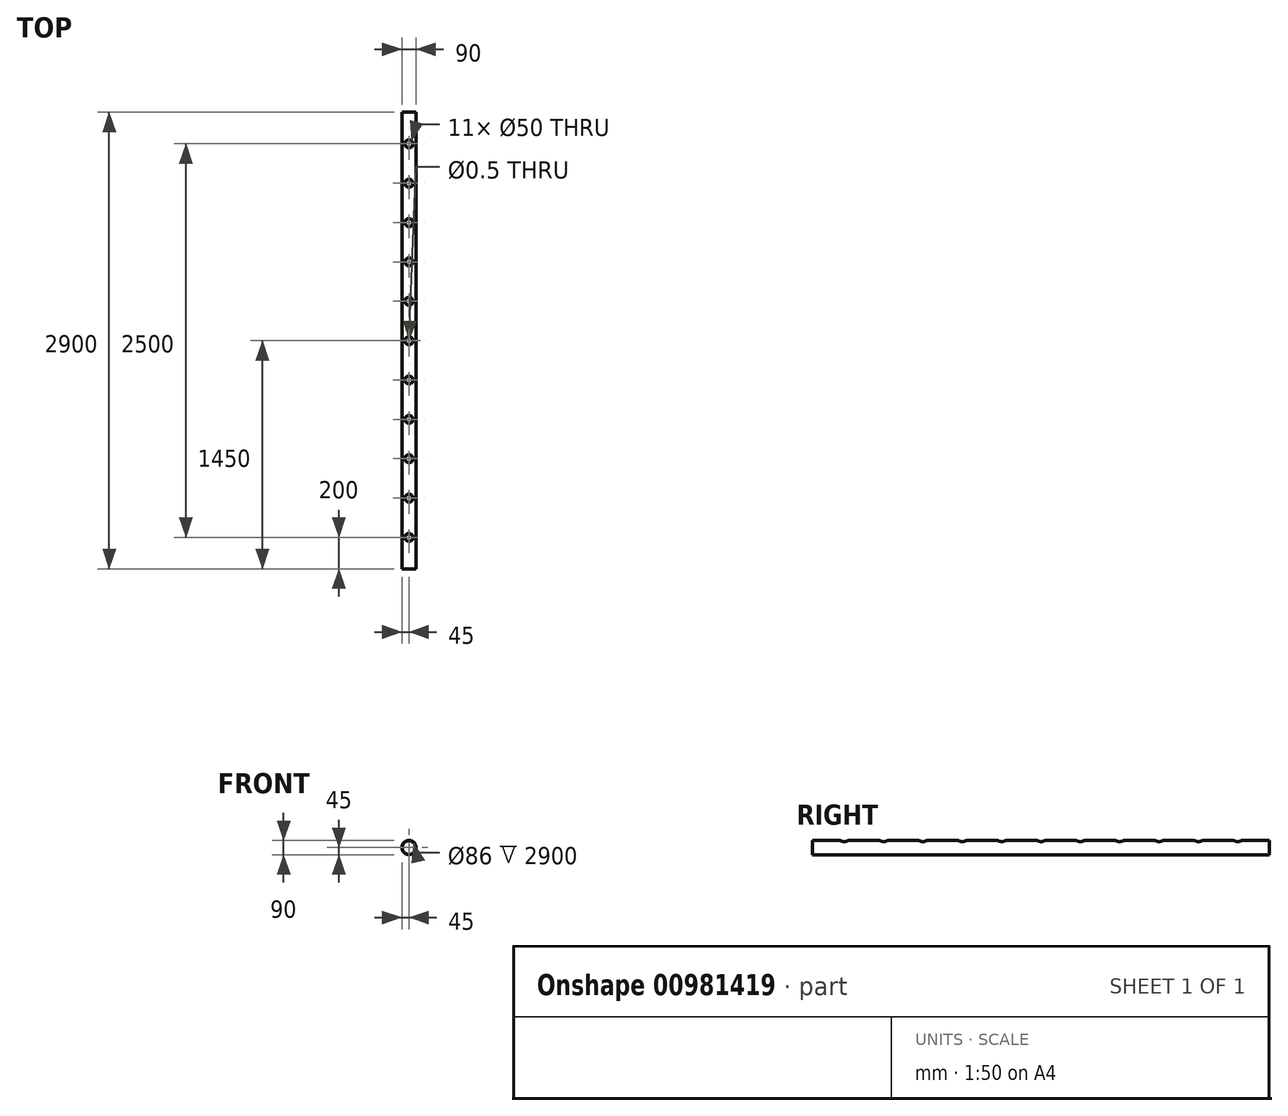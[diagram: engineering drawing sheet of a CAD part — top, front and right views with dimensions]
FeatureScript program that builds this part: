
annotation { "Feature Type Name" : "Feature", "Feature Type Description" : "" }
export const myFeature = defineFeature(function(context is Context, id is Id, definition is map)
    precondition{}
    {
        {
            var Q0;
            Q0=qCreatedBy(makeId("Front.planeOp"),FACE);
            var sketch = newSketch(context, id + "F0", { "sketchPlane" : qUnion([Q0])});
            skCircle(sketch, "E0", {"center": v(0, 0) * mm, "radius": 45 * mm});
            skCircle(sketch, "E1.0", {"center": v(0, 0) * mm, "radius": 43 * mm});
            skSolve(sketch);
        }
        {
            var Q0;
            Q0=qSketchRegion(id+"F0",true);
            extrude(context, id + "F1", {"entities" : qUnion([Q0]), "endBound" : BoundingType.SYMMETRIC, "depth" : 2900 * mm, "offsetDistance" : 25 * mm});
        }
        {
            var Q0;
            Q0=qCreatedBy(makeId("Top.planeOp"),FACE);
            cPlane(context, id + "F2", {"entities" : qUnion([Q0]), "cplaneType" : CPlaneType.OFFSET, "offset" : 45 * mm, "width" : 150 * mm, "height" : 150 * mm});
        }
        {
            var Q0;
            Q0=qCreatedBy(id+"F2.planeOp",FACE);
            var sketch = newSketch(context, id + "F3", { "sketchPlane" : qUnion([Q0])});
            skPoint(sketch, "E2", {"position": v(0, -1250) * mm});
            skPoint(sketch, "E3", {"position": v(0, -1000) * mm});
            skPoint(sketch, "E4", {"position": v(0, -750) * mm});
            skPoint(sketch, "E5", {"position": v(0, -500) * mm});
            skPoint(sketch, "E6", {"position": v(0, -250) * mm});
            skPoint(sketch, "E7", {"position": v(0, 0) * mm});
            skPoint(sketch, "E8", {"position": v(0, 250) * mm});
            skPoint(sketch, "E9", {"position": v(0, 500) * mm});
            skPoint(sketch, "E10", {"position": v(0, 750) * mm});
            skPoint(sketch, "E11", {"position": v(0, 1000) * mm});
            skPoint(sketch, "E12", {"position": v(0, 1250) * mm});
            skSolve(sketch);
        }
        {
            var Q0;
            Q0=sQuery(id+"F3.wireOp",VERTEX,"E2");
            var Q1;
            Q1=sQuery(id+"F3.wireOp",VERTEX,"E3");
            var Q2;
            Q2=sQuery(id+"F3.wireOp",VERTEX,"E4");
            var Q3;
            Q3=sQuery(id+"F3.wireOp",VERTEX,"E5");
            var Q4;
            Q4=sQuery(id+"F3.wireOp",VERTEX,"E6");
            var Q5;
            Q5=sQuery(id+"F3.wireOp",VERTEX,"E7");
            var Q6;
            Q6=sQuery(id+"F3.wireOp",VERTEX,"E8");
            var Q7;
            Q7=sQuery(id+"F3.wireOp",VERTEX,"E9");
            var Q8;
            Q8=sQuery(id+"F3.wireOp",VERTEX,"E10");
            var Q9;
            Q9=sQuery(id+"F3.wireOp",VERTEX,"E11");
            var Q10;
            Q10=sQuery(id+"F3.wireOp",VERTEX,"E12");
            var Q11;
            Q11=sQuery(id+"F3.wireOp",VERTEX,"98bfdb10-889b-4535-8e33-4c68f40e96e9");
            var Q12;
            Q12=sQuery(id+"F3.wireOp",VERTEX,"d6d3cdd6-09bc-4208-8bfb-94afde8f0a46");
            var Q13;
            Q13=sQuery(id+"F3.wireOp",VERTEX,"734153c6-2249-4abd-a6b6-f48a35ac855c");
            var Q14;
            Q14=sQuery(id+"F3.wireOp",VERTEX,"46e0f81d-7a3e-4eb5-89d9-9d338da62cf5");
            var Q15;
            Q15=sQuery(id+"F3.wireOp",VERTEX,"f4cd902c-7ee6-44a1-aa6d-15636b985a91");
            var Q16;
            Q16=sQuery(id+"F3.wireOp",VERTEX,"a0becd45-3f8c-473a-b9c5-eca89ffffb86");
            var Q17;
            Q17=sQuery(id+"F3.wireOp",VERTEX,"449d03d7-6090-459a-adaf-9611daa20e82");
            var Q18;
            Q18=sQuery(id+"F3.wireOp",VERTEX,"1d2369e2-f7b6-45cb-9ac7-ef4d2139859a");
            var Q19;
            Q19=sQuery(id+"F3.wireOp",VERTEX,"4217ffee-23aa-4e57-b56b-1031955cdd20");
            var Q20;
            Q20=sQuery(id+"F3.wireOp",VERTEX,"f9e667d2-43f0-46cb-85dd-7700daad2ab1");
            var Q21;
            Q21=sQuery(id+"F3.wireOp",VERTEX,"a141cc4f-d6fa-4136-a428-d91cc8b08e23");
            var Q22;
            Q22=sQuery(id+"F3.wireOp",VERTEX,"6950c5e6-caf7-4953-8c5b-56709a9cffe9");
            var Q23;
            Q23=sQuery(id+"F3.wireOp",VERTEX,"1581daf2-9304-4365-a3cc-e960652a3bf4");
            var Q24;
            Q24=sQuery(id+"F3.wireOp",VERTEX,"25a0b738-50ad-46bb-ba52-db4eb22869ea");
            var Q25;
            Q25=sQuery(id+"F3.wireOp",VERTEX,"23c6b068-1da5-4682-a93c-07f6e733a235");
            var Q26;
            Q26=sQuery(id+"F3.wireOp",VERTEX,"77491461-51bd-4097-a69a-b50156a0fef7");
            var Q27;
            Q27=sQuery(id+"F3.wireOp",VERTEX,"89e2eaf9-af87-4198-a739-5b01357332c3");
            var Q28;
            Q28=sQuery(id+"F3.wireOp",VERTEX,"a31ac070-19d1-4092-b391-6f630edb761b");
            var Q29;
            Q29=makeQuery(id+"F1.opExtrude","SWEPT_BODY",BODY,{"disambiguationData":[OSD([sQuery(id+"F0.wireOp",EDGE,"E0"),sQuery(id+"F0.wireOp",EDGE,"E1.0")])]});
            hole(context, id + "F4", {"style" : HoleStyle.SIMPLE, "endStyle" : HoleEndStyle.BLIND, "holeDiameter" : 50 * mm, "majorDiameter" : 5 * mm, "holeDepth" : 50 * mm, "isTappedThrough" : true, "tappedDepth" : 12 * mm, "tapClearance" : 3, "startFromSketch" : true, "locations" : qUnion([Q0, Q1, Q2, Q3, Q4, Q5, Q6, Q7, Q8, Q9, Q10, Q11, Q12, Q13, Q14, Q15, Q16, Q17, Q18, Q19, Q20, Q21, Q22, Q23, Q24, Q25, Q26, Q27, Q28]), "scope" : qUnion([Q29])});
        }
        {
            var Q0;
            Q0=qCreatedBy(makeId("Top.planeOp"),FACE);
            var sketch = newSketch(context, id + "F5", { "sketchPlane" : qUnion([Q0])});
            skPoint(sketch, "E13", {"position": v(0, 0) * mm});
            skSolve(sketch);
        }
        {
            var Q0;
            Q0=sQuery(id+"F5.wireOp",VERTEX,"E13");
            var Q1;
            Q1=makeQuery(id+"F1.opExtrude","SWEPT_BODY",BODY,{"disambiguationData":[OSD([sQuery(id+"F0.wireOp",EDGE,"E0"),sQuery(id+"F0.wireOp",EDGE,"E1.0")])]});
            hole(context, id + "F6", {"style" : HoleStyle.SIMPLE, "endStyle" : HoleEndStyle.BLIND, "holeDiameter" : 0.5 * mm, "majorDiameter" : 5 * mm, "holeDepth" : 50 * mm, "isTappedThrough" : true, "tappedDepth" : 12 * mm, "tapClearance" : 3, "startFromSketch" : true, "locations" : qUnion([Q0]), "scope" : qUnion([Q1])});
        }
    });
